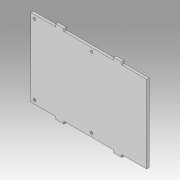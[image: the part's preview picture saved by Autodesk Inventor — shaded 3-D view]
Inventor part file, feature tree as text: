
AUTODESK INVENTOR PART (.ipt)
format: ipt  version: 2019.3 (Build 233278000, 278)  size: 118,272 bytes
history: native  units: mm
features: extrude x1, sketch x1
ambient origin geometry x8: Origin, YZ Plane, XZ Plane, XY Plane, X Axis, Y Axis, Z Axis, Center Point
bodies: Solid1 (feature_tree)
feature tree (2):
  extrude  "Extrusion1"  Depth=3.0mm
  sketch  "Sketch1"  dims[d0=3.1mm d1=85.0mm d2=69.0mm d3=94.0mm d4=4.5mm d5=4.5mm d6=4.5mm d7=140.0mm d12=30.0mm d13=30.0mm d14=3.0mm d15=0.0mm d16=10.0mm d17=3.0mm d18=10.0mm d19=3.0mm]
